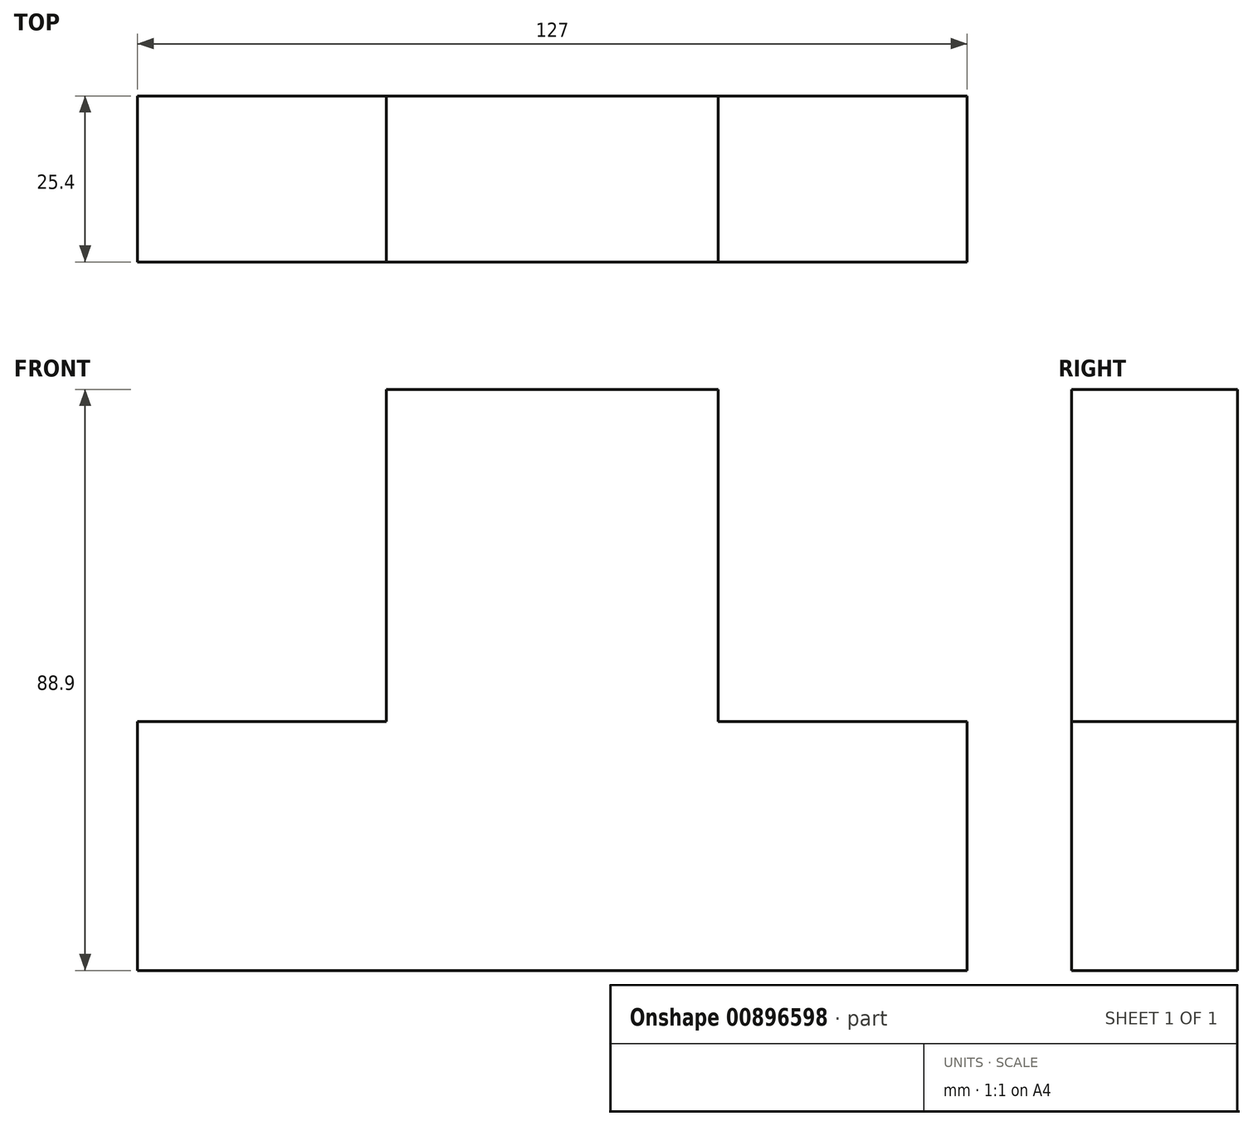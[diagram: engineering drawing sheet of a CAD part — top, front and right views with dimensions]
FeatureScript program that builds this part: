
annotation { "Feature Type Name" : "Feature", "Feature Type Description" : "" }
export const myFeature = defineFeature(function(context is Context, id is Id, definition is map)
    precondition{}
    {
        {
            var Q0;
            Q0=qCreatedBy(makeId("Front.planeOp"),FACE);
            var sketch = newSketch(context, id + "F0", { "sketchPlane" : qUnion([Q0])});
            skLineSegment(sketch, "E0", {"start": v(-75.48, 0) * mm, "end": v(51.52, 0) * mm});
            skLineSegment(sketch, "E1", {"start": v(-75.48, 0) * mm, "end": v(-75.48, 38.1) * mm});
            skLineSegment(sketch, "E2", {"start": v(51.52, 0) * mm, "end": v(51.52, 38.1) * mm});
            skLineSegment(sketch, "E3", {"start": v(-75.48, 38.1) * mm, "end": v(-37.38, 38.1) * mm});
            skLineSegment(sketch, "E4", {"start": v(51.52, 38.1) * mm, "end": v(13.42, 38.1) * mm});
            skLineSegment(sketch, "E5", {"start": v(13.42, 38.1) * mm, "end": v(13.42, 88.9) * mm});
            skLineSegment(sketch, "E6", {"start": v(-37.38, 38.1) * mm, "end": v(-37.38, 88.9) * mm});
            skLineSegment(sketch, "E7", {"start": v(13.42, 88.9) * mm, "end": v(-37.38, 88.9) * mm});
            skSolve(sketch);
        }
        {
            var Q0;
            Q0 = qSketchRegion(id + "F0", true);
            extrude(context, id + "F1", {"entities" : qUnion([Q0]), "depth" : 25.4 * mm, "offsetDistance" : 25.4 * mm});
        }
    });
